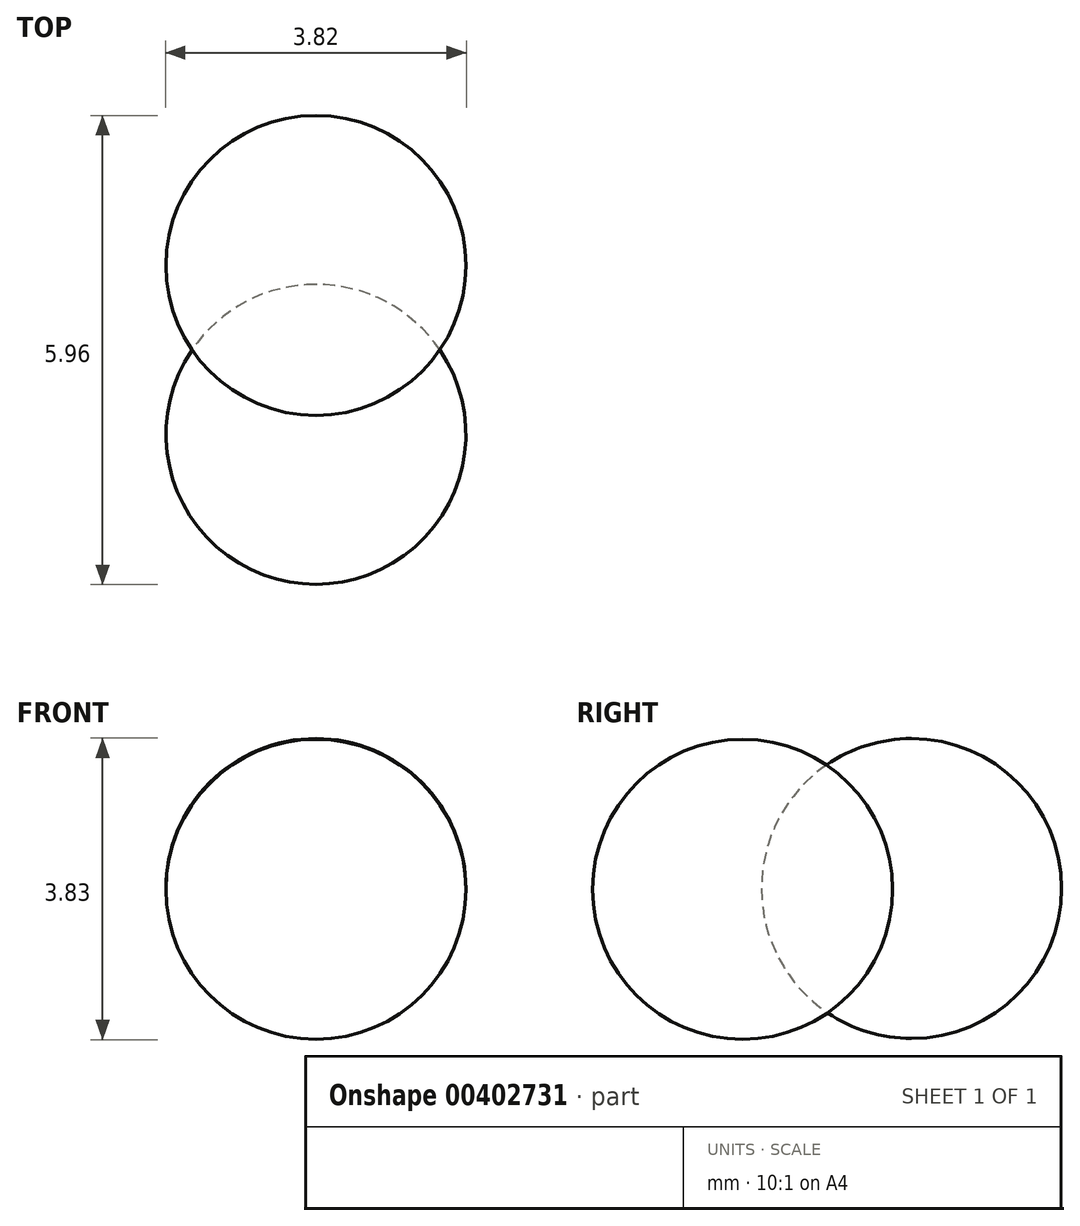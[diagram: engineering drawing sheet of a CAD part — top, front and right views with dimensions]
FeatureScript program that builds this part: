
annotation { "Feature Type Name" : "Feature", "Feature Type Description" : "" }
export const myFeature = defineFeature(function(context is Context, id is Id, definition is map)
    precondition{}
    {
        {
            var Q0;
            Q0=qCreatedBy(makeId("Right.planeOp"),FACE);
            var sketch = newSketch(context, id + "F0", { "sketchPlane" : qUnion([Q0])});
            skLineSegment(sketch, "E0", {"start": v(0, 9.46) * mm, "end": v(0, -13.24) * mm});
            skCircle(sketch, "E1", {"center": v(0, 0) * mm, "radius": 3.81 * mm});
            skSolve(sketch);
        }
        {
            var Q0;
            {var subQ0=sQuery(id+"F0.wireOp",EDGE,"E1");var subQ1=sQuery(id+"F0.wireOp",EDGE,"E0");var subQ2=makeQuery(id+"F0.imprint","INTERSECT",VERTEX,{"disambiguationData":[OD(0.0)],"derivedFrom":[subQ1,subQ0]});Q0=makeQuery(id+"F0.imprint","IMPRINT",FACE,{"disambiguationData":[TD([[makeQuery(id+"F0.imprint","IMPRINT",EDGE,{"disambiguationData":[TD([[subQ2,1.0]])],"derivedFrom":subQ1}),-1.0]])]});}
            var Q1;
            Q1=sQuery(id+"F0.wireOp",EDGE,"E0");
            revolve(context, id + "F1", {"entities" : qUnion([Q0]), "axis" : qUnion([Q1]), "revolveType" : RevolveType.FULL});
        }
        {
            var Q0;
            Q0=qCreatedBy(makeId("Right.planeOp"),FACE);
            var sketch = newSketch(context, id + "F2", { "sketchPlane" : qUnion([Q0])});
            skLineSegment(sketch, "E2", {"start": v(4.3, 13.13) * mm, "end": v(4.3, -13.09) * mm});
            skCircle(sketch, "E3", {"center": v(4.3, 0.02) * mm, "radius": 3.8 * mm});
            skSolve(sketch);
        }
        {
            var Q0;
            {var subQ0=sQuery(id+"F2.wireOp",EDGE,"E3");var subQ1=sQuery(id+"F2.wireOp",EDGE,"E2");var subQ2=makeQuery(id+"F2.imprint","INTERSECT",VERTEX,{"disambiguationData":[OD(0.0)],"derivedFrom":[subQ1,subQ0]});Q0=makeQuery(id+"F2.imprint","IMPRINT",FACE,{"disambiguationData":[TD([[makeQuery(id+"F2.imprint","IMPRINT",EDGE,{"disambiguationData":[TD([[subQ2,1.0]])],"derivedFrom":subQ1}),-1.0]])]});}
            var Q1;
            Q1=sQuery(id+"F2.wireOp",EDGE,"E2");
            revolve(context, id + "F3", {"entities" : qUnion([Q0]), "axis" : qUnion([Q1]), "revolveType" : RevolveType.FULL});
        }
        {
            var Q0;
            Q0=makeQuery(id+"F3.opRevolve","SWEPT_BODY",BODY,{"disambiguationData":[OSD([sQuery(id+"F2.wireOp",EDGE,"E2"),sQuery(id+"F2.wireOp",EDGE,"E3")])]});
            var Q1;
            Q1=makeQuery(id+"F1.opRevolve","SWEPT_BODY",BODY,{"disambiguationData":[OSD([sQuery(id+"F0.wireOp",EDGE,"E0"),sQuery(id+"F0.wireOp",EDGE,"E1")])]});
            var Q2;
            Q2=qCreatedBy(makeId("Origin.pointOp"),VERTEX);
            transform(context, id + "F4", {"entities" : qUnion([Q0, Q1]), "transformType" : TransformType.SCALE_UNIFORMLY, "scale" : .5, "scalePoint" : qUnion([Q2]), "makeCopy" : false});
        }
    });
